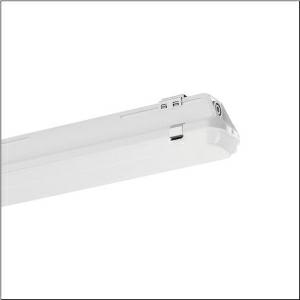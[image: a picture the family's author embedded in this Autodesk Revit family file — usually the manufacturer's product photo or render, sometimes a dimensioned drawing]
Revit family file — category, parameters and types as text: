
# Revit family: monsun_r__12_51fp10ep460h_76e9
name_source: partatom
category: Lighting Fixtures
units: mm (PartAtom-declared; Revit-internal decimal feet)

## family parameters
Cut with Voids When Loaded = No
Host = Face
Light Source = No
Part Type = Normal
Room Calculation Point = No
Round Connector Dimension = Use Diameter
Shared = No

## types (1)
- --- (1 x LED, 6050 lm, 34.6 W, 4000K)
    Apparent Load = 35 VA
    CIE Flux Codes = 47 77 93 94 100
    Color Rendering = 80
    Color Temperature = 4000K
    Default Elevation = 1800 mm
    Description = Monsun® 12, damp-proof luminaire, chain hanger, primary optical cover: enclosure, of PMMA, light emission: direct distribution, primary light characteristic: symmetric, installation type: suspended mounting, surface-mounted, horizontal mounting, vertical mounting, LED rated luminous flux: 6.050 lm, light colour: 840, colour temperature: 4000K, control gear: ECG DALI, with terminal, 5-pole, max. 2.5mm², mains connection: 220..240V, AC, 50/60Hz, rated input power: 35W, luminaire housing, of glass-fibre reinforced polyester, uncoated, bright grey, length: 1.590 mm, width: 90 mm, height: 88mm, clip for enclosure, of stainless steel (V2A), ceiling mounting element, of stainless steel (V2A), chain hanger, of stainless steel (V2A), protection rating (complete): IP66, insulation class (complete): insulation class I (protective earthing), certification: CE, ENEC, VDE, protection symbol: D, impact resistance: IK04, permissible ambient temperature for indoor applications: -25..+40°C, standard: EN 50419, EN 60598-2-1, no direct snow, no direct sun, no direct rain, for indoor or canopied outdoor use, corresponds to IFS (International Featured Standards) requirements for safety and quality in the food industry, for animal farming (ammonia tested): for use in cowhouse, pig house, horse-stables... (not for use in poultry stables), AT max for animal farming = 40°C, packaging unit: 1 piece
    Height = 89 mm
    Lamp = 1 x LED
    Lamp Light Flux = 6050 lm
    Lamp Power = 34.6 W
    Lamp count = 1
    Length = 1590 mm
    Luminous efficacy = 175 lm/W
    Manufacturer = Siteco
    ModVariant = No
    Model = 51FP10EP460H
    Mounting Place = Ceiling
    Mounting Type = Pendant
    Number of Poles = 1
    OnlyDefault = Yes
    Power Factor = 1
    Product Name = Monsun® 12
    Product group = damp-proof luminaire | ceiling pendant
    ProductGroupID = 908
    Protection Class = Protection class I
    Protection Degree = IP 66
    RLX_Detail_Level = 1
    RlxData = <blob elided: 91893 chars, md5=1fe1aa45>
    Socket = socket
    Standby Power = 0 W
    System Light Flux = 6050 lm
    System Power = 35 W
    Type Comments = factory setting: luminous flux: 100 % | dim-lin: 254 | 232 mA
    Type Image = l_1004748.jpg
    URL = http://relux.com
    VarID = @adj_136255
    Voltage = 0 V
    Weight = 0.00 kg
    Width = 90 mm

## geometry (parser evidence)
native form markers: Blend x4, Sweep x14
no freeform markers — native parametric forms only
